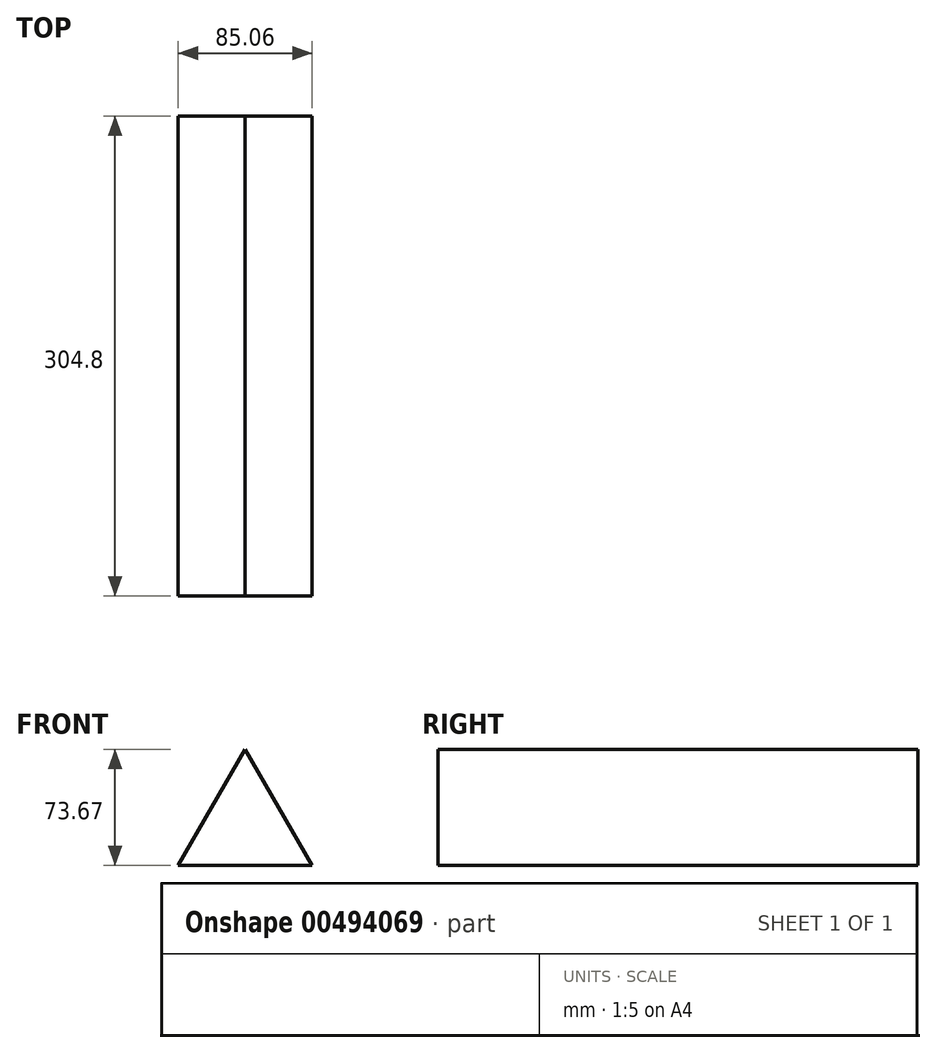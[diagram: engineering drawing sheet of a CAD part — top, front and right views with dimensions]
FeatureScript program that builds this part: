
annotation { "Feature Type Name" : "Feature", "Feature Type Description" : "" }
export const myFeature = defineFeature(function(context is Context, id is Id, definition is map)
    precondition{}
    {
        {
            var Q0;
            Q0=qCreatedBy(makeId("Front.planeOp"),FACE);
            var sketch = newSketch(context, id + "F0", { "sketchPlane" : qUnion([Q0])});
            skCircle(sketch, "E0.cCircle", {"center": v(0, 0) * mm, "radius": 49.11 * mm, "construction": true});
            skLineSegment(sketch, "E0.0", {"start": v(-42.53, -24.56) * mm, "end": v(0, 49.11) * mm});
            skLineSegment(sketch, "E0.1", {"start": v(0, 49.11) * mm, "end": v(42.53, -24.56) * mm});
            skLineSegment(sketch, "E0.2", {"start": v(42.53, -24.56) * mm, "end": v(-42.53, -24.56) * mm});
            skSolve(sketch);
        }
        {
            var Q0;
            Q0 = qSketchRegion(id + "F0", true);
            extrude(context, id + "F1", {"entities" : qUnion([Q0]), "depth" : 304.8 * mm});
        }
    });
